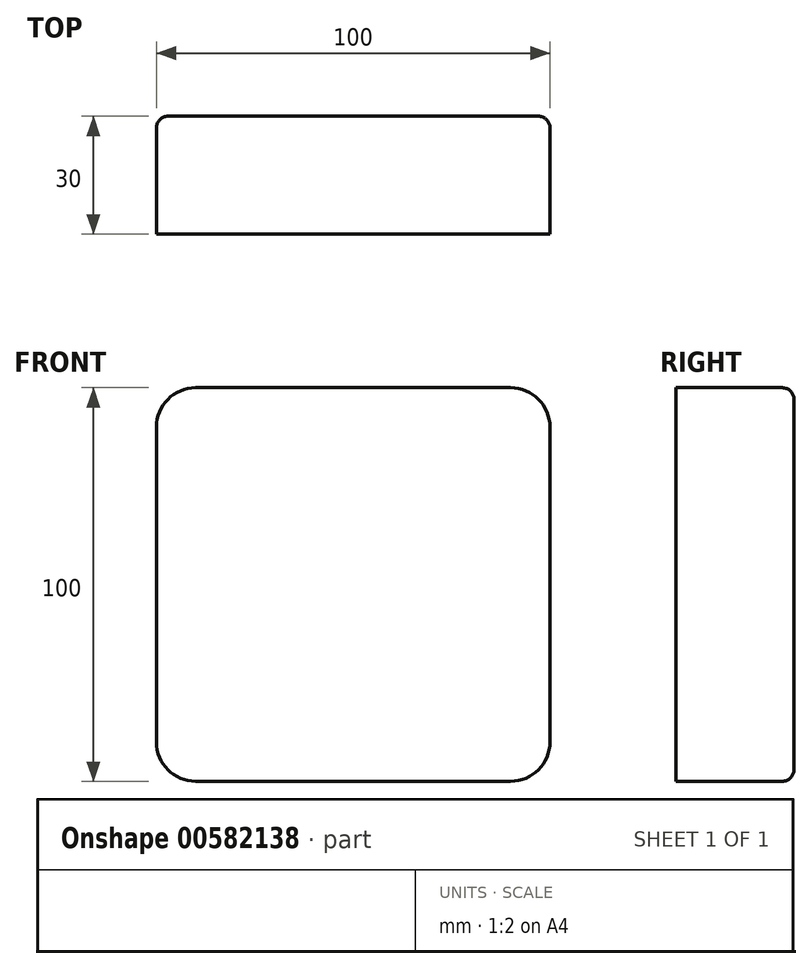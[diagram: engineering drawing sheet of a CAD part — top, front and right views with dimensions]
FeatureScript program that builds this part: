
annotation { "Feature Type Name" : "Feature", "Feature Type Description" : "" }
export const myFeature = defineFeature(function(context is Context, id is Id, definition is map)
    precondition{}
    {
        {
            var Q0;
            Q0=qCreatedBy(makeId("Front.planeOp"),FACE);
            var sketch = newSketch(context, id + "F0", { "sketchPlane" : qUnion([Q0])});
            skLineSegment(sketch, "E0.bottom", {"start": v(0, 0) * mm, "end": v(100, 0) * mm});
            skLineSegment(sketch, "E0.top", {"start": v(0, 100) * mm, "end": v(100, 100) * mm});
            skLineSegment(sketch, "E0.left", {"start": v(0, 0) * mm, "end": v(0, 100) * mm});
            skLineSegment(sketch, "E0.right", {"start": v(100, 0) * mm, "end": v(100, 100) * mm});
            skSolve(sketch);
        }
        {
            var Q0;
            Q0 = qSketchRegion(id + "F0", true);
            extrude(context, id + "F1", {"entities" : qUnion([Q0]), "depth" : 30 * mm, "offsetDistance" : 25 * mm});
        }
        {
            var Q0;
            Q0=makeQuery(id+"F1.opExtrude","SWEPT_EDGE",EDGE,{"disambiguationData":[OSD([sQuery(id+"F0.wireOp",EDGE,"E0.top"),sQuery(id+"F0.wireOp",EDGE,"E0.left")])]});
            var Q1;
            Q1=makeQuery(id+"F1.opExtrude","SWEPT_EDGE",EDGE,{"disambiguationData":[OSD([sQuery(id+"F0.wireOp",EDGE,"E0.bottom"),sQuery(id+"F0.wireOp",EDGE,"E0.left")])]});
            var Q2;
            Q2=makeQuery(id+"F1.opExtrude","SWEPT_EDGE",EDGE,{"disambiguationData":[OSD([sQuery(id+"F0.wireOp",EDGE,"E0.bottom"),sQuery(id+"F0.wireOp",EDGE,"E0.right")])]});
            var Q3;
            Q3=makeQuery(id+"F1.opExtrude","SWEPT_EDGE",EDGE,{"disambiguationData":[OSD([sQuery(id+"F0.wireOp",EDGE,"E0.top"),sQuery(id+"F0.wireOp",EDGE,"E0.right")])]});
            fillet(context, id + "F2", {"entities" : qUnion([Q0, Q1, Q2, Q3]), "radius" : 10 * mm, "tangentPropagation" : true, "allowEdgeOverflow" : false});
        }
        {
            var Q0;
            Q0=makeQuery(id+"F1.opExtrude","CAP_FACE",FACE,{"disambiguationData":[OSD([sQuery(id+"F0.wireOp",EDGE,"E0.bottom"),sQuery(id+"F0.wireOp",EDGE,"E0.top"),sQuery(id+"F0.wireOp",EDGE,"E0.left"),sQuery(id+"F0.wireOp",EDGE,"E0.right")])],"isStart":true});
            fillet(context, id + "F3", {"entities" : qUnion([Q0]), "radius" : 3 * mm, "tangentPropagation" : true, "allowEdgeOverflow" : false});
        }
    });
